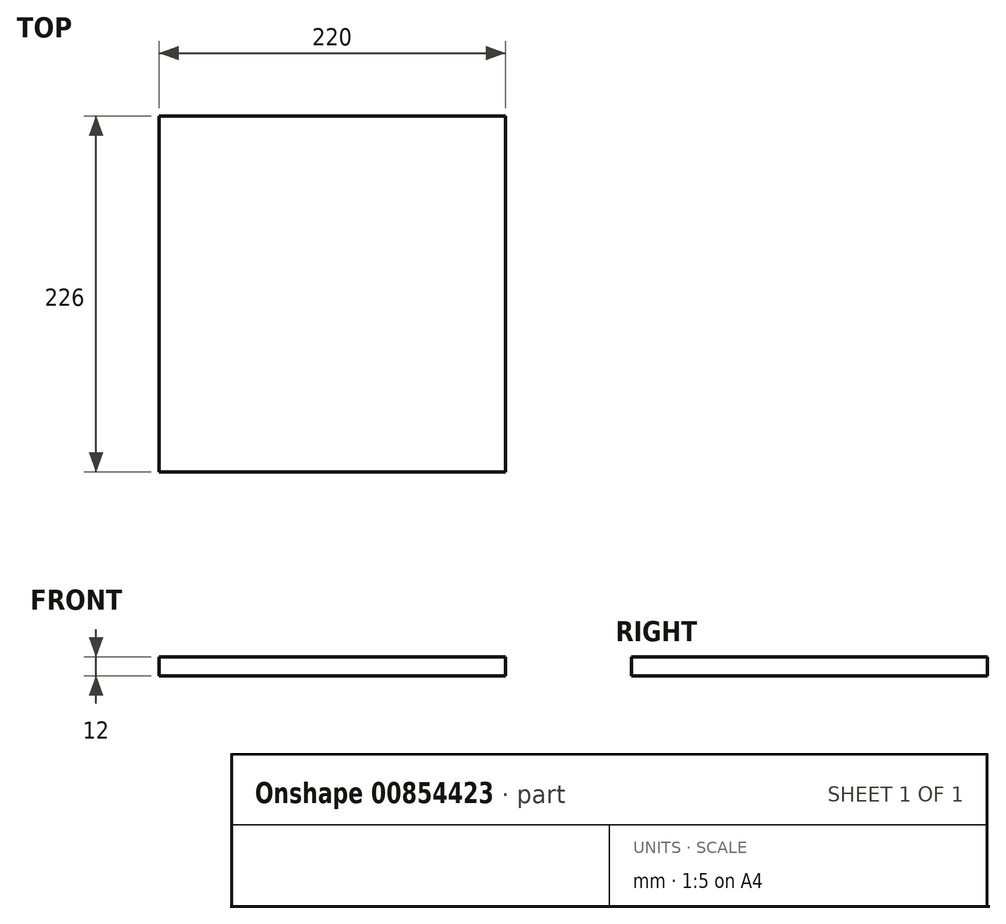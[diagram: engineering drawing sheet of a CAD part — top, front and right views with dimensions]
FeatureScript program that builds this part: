
annotation { "Feature Type Name" : "Feature", "Feature Type Description" : "" }
export const myFeature = defineFeature(function(context is Context, id is Id, definition is map)
    precondition{}
    {
        {
            var Q0;
            Q0=qCreatedBy(makeId("Top.planeOp"),FACE);
            var sketch = newSketch(context, id + "F0", { "sketchPlane" : qUnion([Q0])});
            skLineSegment(sketch, "E0.bottom", {"start": v(-122, 122) * mm, "end": v(122, 122) * mm});
            skLineSegment(sketch, "E0.top", {"start": v(-122, -122) * mm, "end": v(122, -122) * mm});
            skLineSegment(sketch, "E0.left", {"start": v(-122, 122) * mm, "end": v(-122, -122) * mm});
            skLineSegment(sketch, "E0.right", {"start": v(122, 122) * mm, "end": v(122, -122) * mm});
            skPoint(sketch, "E0.middle", {"position": v(0, 0) * mm});
            skSolve(sketch);
        }
        {
            var Q0;
            Q0 = qSketchRegion(id + "F0", true);
            extrude(context, id + "F1", {"entities" : qUnion([Q0]), "depth" : 12 * mm, "offsetDistance" : 25.4 * mm});
        }
        {
            var Q0;
            Q0=makeQuery(id+"F1.opExtrude","SWEPT_BODY",BODY,{"disambiguationData":[OSD([sQuery(id+"F0.wireOp",EDGE,"E0.bottom"),sQuery(id+"F0.wireOp",EDGE,"E0.top"),sQuery(id+"F0.wireOp",EDGE,"E0.left"),sQuery(id+"F0.wireOp",EDGE,"E0.right")])]});
            deleteBodies(context, id + "F2", {"entities" : qUnion([Q0])});
        }
        {
            var Q0;
            Q0=qCreatedBy(makeId("Top.planeOp"),FACE);
            var sketch = newSketch(context, id + "F3", { "sketchPlane" : qUnion([Q0])});
            skLineSegment(sketch, "E1.bottom", {"start": v(-110, 113) * mm, "end": v(110, 113) * mm});
            skLineSegment(sketch, "E1.top", {"start": v(-110, -113) * mm, "end": v(110, -113) * mm});
            skLineSegment(sketch, "E1.left", {"start": v(-110, 113) * mm, "end": v(-110, -113) * mm});
            skLineSegment(sketch, "E1.right", {"start": v(110, 113) * mm, "end": v(110, -113) * mm});
            skPoint(sketch, "E1.middle", {"position": v(0, 0) * mm});
            skSolve(sketch);
        }
        {
            var Q0;
            Q0 = qSketchRegion(id + "F3", true);
            extrude(context, id + "F4", {"entities" : qUnion([Q0]), "depth" : 12 * mm, "offsetDistance" : 25.4 * mm});
        }
    });
